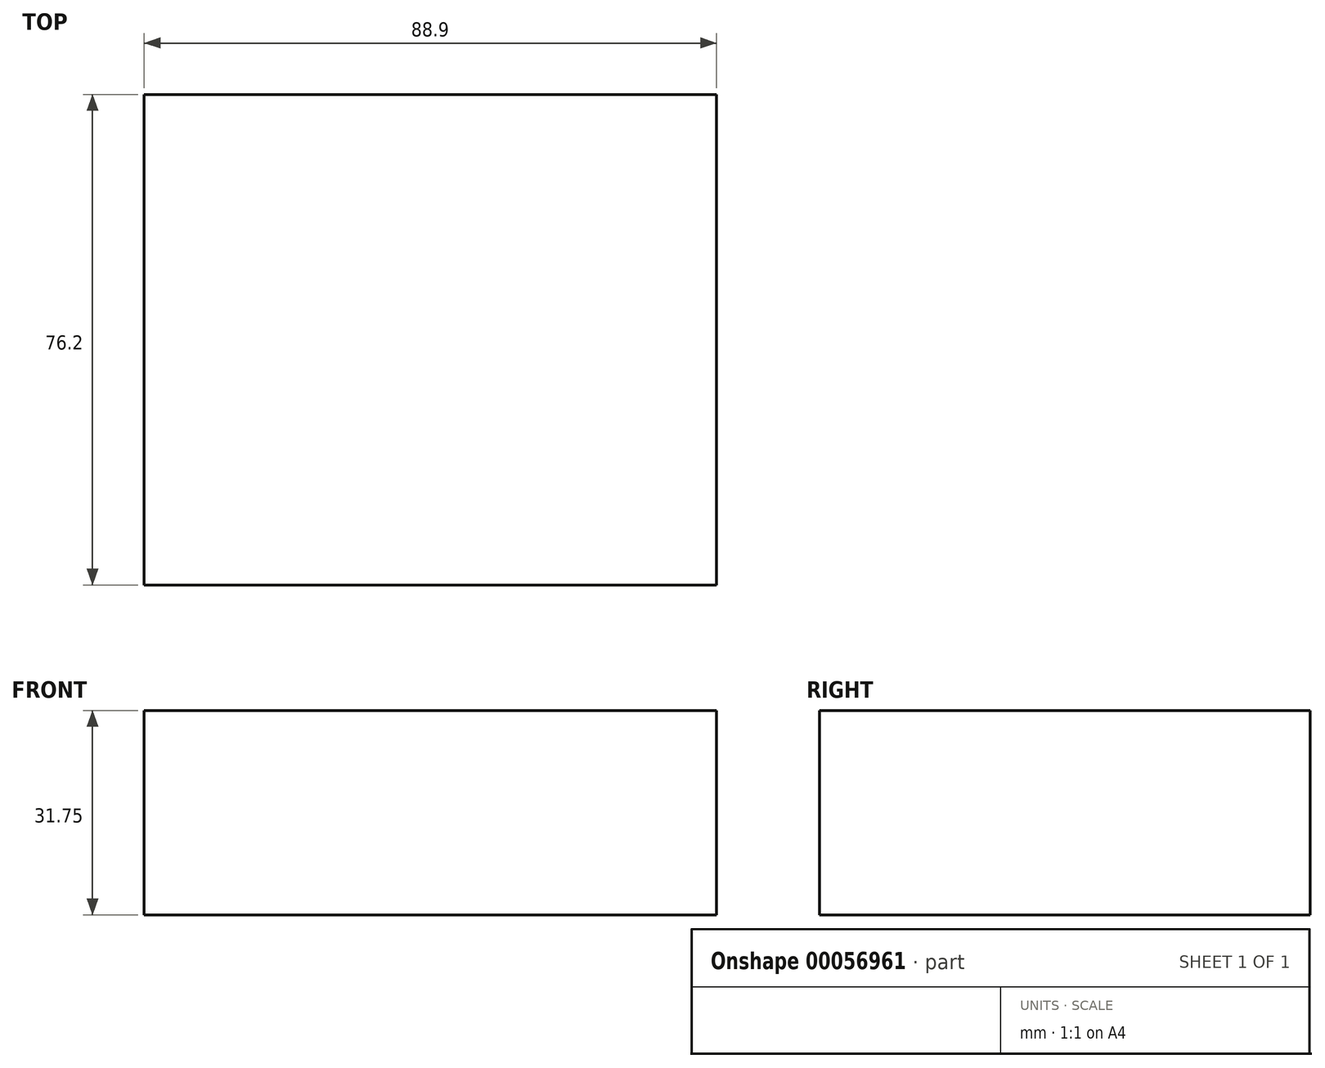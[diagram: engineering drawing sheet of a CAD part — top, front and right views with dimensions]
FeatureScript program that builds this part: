
annotation { "Feature Type Name" : "Feature", "Feature Type Description" : "" }
export const myFeature = defineFeature(function(context is Context, id is Id, definition is map)
    precondition{}
    {
        {
            var Q0;
            Q0=qCreatedBy(makeId("Front.planeOp"),FACE);
            var sketch = newSketch(context, id + "F0", { "sketchPlane" : qUnion([Q0])});
            skLineSegment(sketch, "E0.bottom", {"start": v(0, 0) * mm, "end": v(88.9, 0) * mm});
            skLineSegment(sketch, "E0.top", {"start": v(0, 31.75) * mm, "end": v(88.9, 31.75) * mm});
            skLineSegment(sketch, "E0.left", {"start": v(0, 0) * mm, "end": v(0, 31.75) * mm});
            skLineSegment(sketch, "E0.right", {"start": v(88.9, 0) * mm, "end": v(88.9, 31.75) * mm});
            skSolve(sketch);
        }
        {
            var Q0;
            Q0=makeQuery(id+"F0.imprint","IMPRINT",FACE,{"disambiguationData":[TD([[makeQuery(id+"F0.imprint","IMPRINT",EDGE,{"derivedFrom":sQuery(id+"F0.wireOp",EDGE,"E0.bottom")}),1.0]])]});
            extrude(context, id + "F1", {"entities" : qUnion([Q0]), "depth" : 76.2 * mm});
        }
    });
